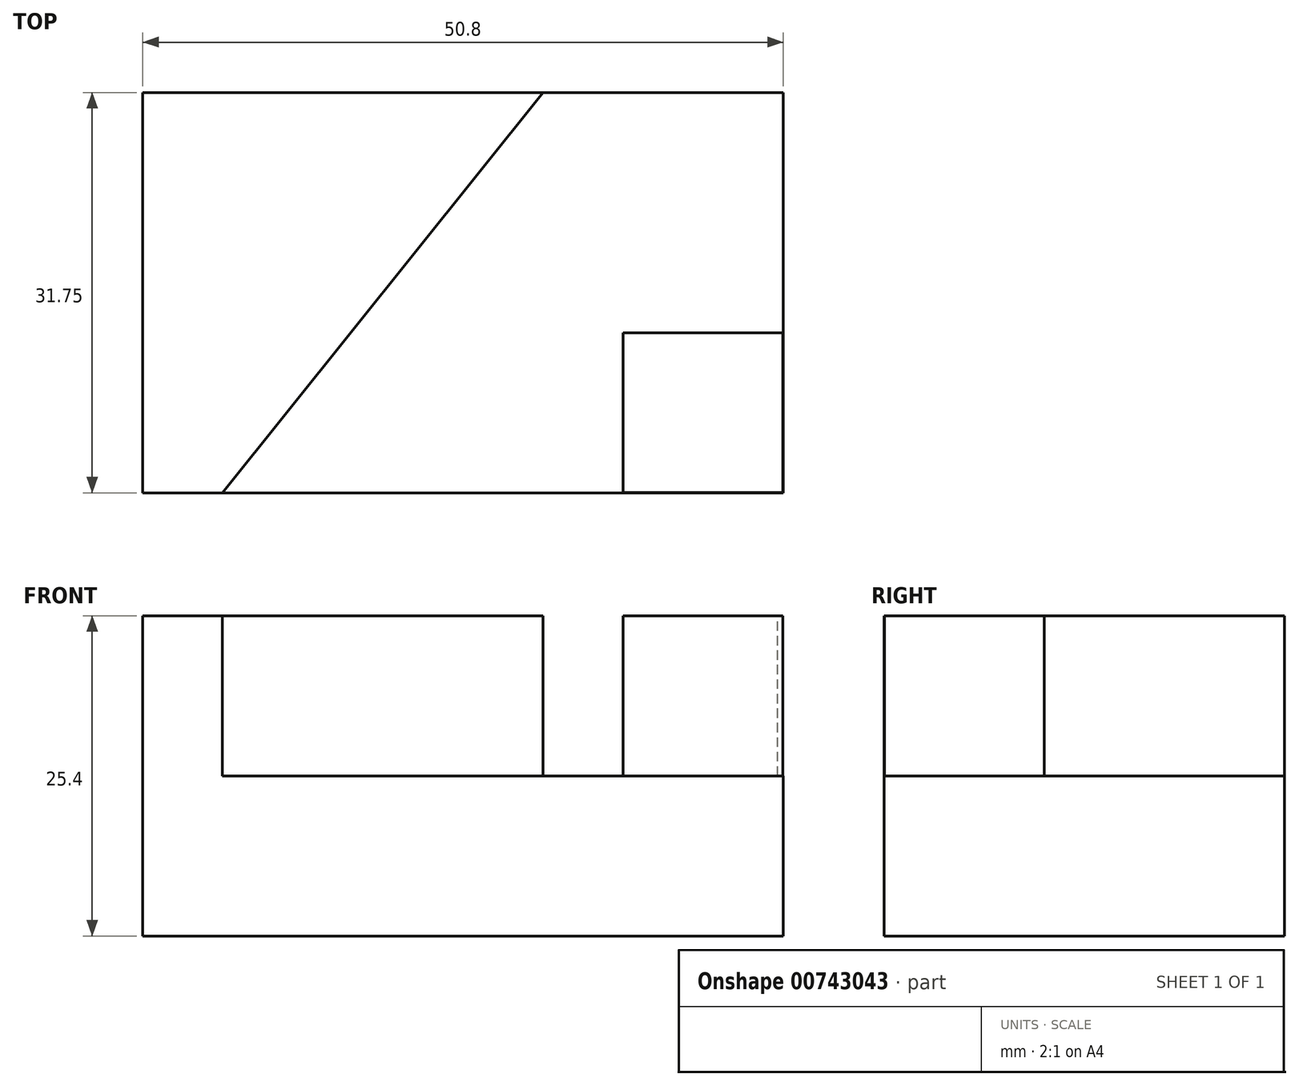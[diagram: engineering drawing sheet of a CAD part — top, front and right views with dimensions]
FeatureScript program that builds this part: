
annotation { "Feature Type Name" : "Feature", "Feature Type Description" : "" }
export const myFeature = defineFeature(function(context is Context, id is Id, definition is map)
    precondition{}
    {
        {
            var Q0;
            Q0=qCreatedBy(makeId("Front.planeOp"),FACE);
            var sketch = newSketch(context, id + "F0", { "sketchPlane" : qUnion([Q0])});
            skLineSegment(sketch, "E0", {"start": v(0, 0) * mm, "end": v(50.8, 0) * mm});
            skLineSegment(sketch, "E1", {"start": v(50.8, 0) * mm, "end": v(50.8, 25.4) * mm});
            skLineSegment(sketch, "E2", {"start": v(50.8, 25.4) * mm, "end": v(0, 25.4) * mm});
            skLineSegment(sketch, "E3", {"start": v(0, 25.4) * mm, "end": v(0, 0) * mm});
            skSolve(sketch);
        }
        {
            var Q0;
            Q0=makeQuery(id+"F0.imprint","IMPRINT",FACE,{"disambiguationData":[TD([[makeQuery(id+"F0.imprint","IMPRINT",EDGE,{"derivedFrom":sQuery(id+"F0.wireOp",EDGE,"E0")}),1.0]])]});
            extrude(context, id + "F1", {"entities" : qUnion([Q0]), "depth" : 31.75 * mm, "offsetDistance" : 25.4 * mm});
        }
        {
            var Q0;
            Q0=makeQuery(id+"F1.opExtrude","SWEPT_FACE",FACE,{"disambiguationData":[OSD([sQuery(id+"F0.wireOp",EDGE,"E1")])]});
            var sketch = newSketch(context, id + "F2", { "sketchPlane" : qUnion([Q0])});
            skLineSegment(sketch, "E4", {"start": v(0, 12.7) * mm, "end": v(-19.05, 12.7) * mm});
            skLineSegment(sketch, "E5", {"start": v(-19.05, 12.7) * mm, "end": v(-19.05, 25.4) * mm});
            skSolve(sketch);
        }
        {
            var Q0;
            {var subQ0=sQuery(id+"F2.wireOp",EDGE,"E4");Q0=makeQuery(id+"F2.imprint","IMPRINT",FACE,{"disambiguationData":[TD([[makeQuery(id+"F2.imprint","IMPRINT",EDGE,{"derivedFrom":subQ0}),-1.0]])]});}
            extrude(context, id + "F3", {"entities" : qUnion([Q0]), "operationType" : NewBodyOperationType.REMOVE, "oppositeDirection" : true, "depth" : 19.05 * mm, "offsetDistance" : 25.4 * mm});
        }
        {
            var Q0;
            Q0=makeQuery(id+"F1.opExtrude","SWEPT_FACE",FACE,{"disambiguationData":[OSD([sQuery(id+"F0.wireOp",EDGE,"E2")])]});
            var sketch = newSketch(context, id + "F4", { "sketchPlane" : qUnion([Q0])});
            skLineSegment(sketch, "E6", {"start": v(6.32, -31.75) * mm, "end": v(31.75, 0) * mm});
            skSolve(sketch);
        }
        {
            var Q0;
            {var subQ3=sQuery(id+"F4.wireOp",EDGE,"E6");Q0=makeQuery(id+"F4.imprint","IMPRINT",FACE,{"disambiguationData":[TD([[makeQuery(id+"F4.imprint","IMPRINT",EDGE,{"derivedFrom":subQ3}),-1.0]])]});}
            var sketch = newSketch(context, id + "F5", { "sketchPlane" : qUnion([Q0])});
            skLineSegment(sketch, "E7", {"start": v(38.1, -31.72) * mm, "end": v(38.1, -18.64) * mm});
            skLineSegment(sketch, "E8", {"start": v(38.1, -31.72) * mm, "end": v(50.77, -31.72) * mm});
            skLineSegment(sketch, "E9", {"start": v(50.77, -31.72) * mm, "end": v(50.77, -19.06) * mm});
            skLineSegment(sketch, "E10", {"start": v(50.77, -19.06) * mm, "end": v(38.1, -18.64) * mm});
            skSolve(sketch);
        }
        {
            var Q0;
            {var subQ6=sQuery(id+"F5.wireOp",EDGE,"E8");Q0=makeQuery(id+"F5.imprint","IMPRINT",FACE,{"disambiguationData":[TD([[makeQuery(id+"F5.imprint","IMPRINT",EDGE,{"derivedFrom":subQ6}),-1.0]])]});}
            extrude(context, id + "F6", {"entities" : qUnion([Q0]), "operationType" : NewBodyOperationType.REMOVE, "oppositeDirection" : true, "depth" : 12.7 * mm, "offsetDistance" : 25.4 * mm});
        }
    });
